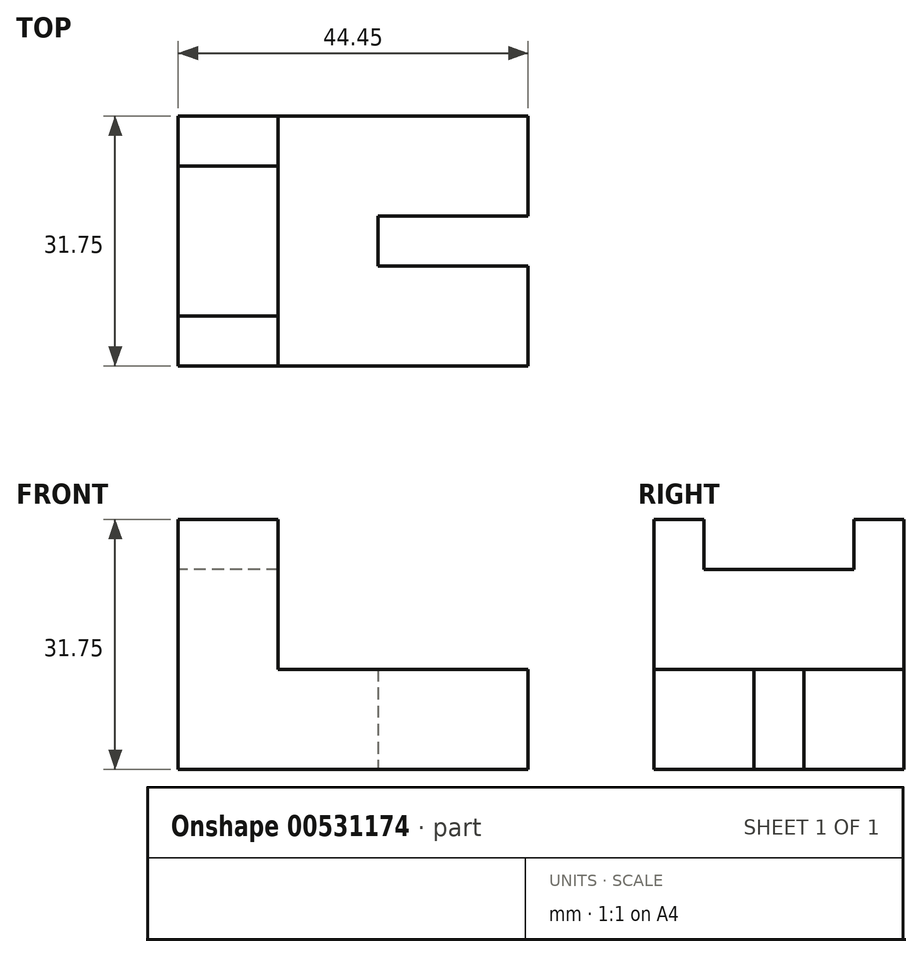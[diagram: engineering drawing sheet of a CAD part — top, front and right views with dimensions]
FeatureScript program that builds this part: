
annotation { "Feature Type Name" : "Feature", "Feature Type Description" : "" }
export const myFeature = defineFeature(function(context is Context, id is Id, definition is map)
    precondition{}
    {
        {
            var Q0;
            Q0=qCreatedBy(makeId("Front.planeOp"),FACE);
            var sketch = newSketch(context, id + "F0", { "sketchPlane" : qUnion([Q0])});
            skLineSegment(sketch, "E0", {"start": v(0, 0) * mm, "end": v(0, 31.75) * mm});
            skLineSegment(sketch, "E1", {"start": v(0, 31.75) * mm, "end": v(12.7, 31.75) * mm});
            skLineSegment(sketch, "E2", {"start": v(12.7, 31.75) * mm, "end": v(12.7, 12.7) * mm});
            skLineSegment(sketch, "E3", {"start": v(12.7, 12.7) * mm, "end": v(44.45, 12.7) * mm});
            skLineSegment(sketch, "E4", {"start": v(44.45, 12.7) * mm, "end": v(44.45, 0) * mm});
            skLineSegment(sketch, "E5", {"start": v(44.45, 0) * mm, "end": v(0, 0) * mm});
            skSolve(sketch);
        }
        {
            var Q0;
            Q0=qCreatedBy(makeId("Right.planeOp"),FACE);
            var sketch = newSketch(context, id + "F1", { "sketchPlane" : qUnion([Q0])});
            skLineSegment(sketch, "E6", {"start": v(0, 0) * mm, "end": v(0, 31.75) * mm});
            skLineSegment(sketch, "E7", {"start": v(0, 31.75) * mm, "end": v(-6.35, 31.75) * mm});
            skLineSegment(sketch, "E8", {"start": v(-6.35, 31.75) * mm, "end": v(-6.35, 25.4) * mm});
            skLineSegment(sketch, "E9", {"start": v(-6.35, 25.4) * mm, "end": v(-25.4, 25.4) * mm});
            skLineSegment(sketch, "E10", {"start": v(-25.4, 25.4) * mm, "end": v(-25.4, 31.75) * mm});
            skLineSegment(sketch, "E11", {"start": v(-25.4, 31.75) * mm, "end": v(-31.75, 31.75) * mm});
            skLineSegment(sketch, "E12", {"start": v(-25.4, 31.75) * mm, "end": v(-6.35, 31.75) * mm});
            skSolve(sketch);
        }
        {
            var Q0;
            Q0=makeQuery(id+"F0.imprint","IMPRINT",FACE,{"disambiguationData":[TD([[makeQuery(id+"F0.imprint","IMPRINT",EDGE,{"derivedFrom":sQuery(id+"F0.wireOp",EDGE,"E0")}),-1.0]])]});
            extrude(context, id + "F2", {"entities" : qUnion([Q0]), "depth" : 31.75 * mm, "offsetDistance" : 25.4 * mm});
        }
        {
            var Q0;
            Q0=makeQuery(id+"F1.imprint","IMPRINT",FACE,{"disambiguationData":[TD([[makeQuery(id+"F1.imprint","IMPRINT",EDGE,{"derivedFrom":sQuery(id+"F1.wireOp",EDGE,"E8")}),-1.0]])]});
            extrude(context, id + "F3", {"entities" : qUnion([Q0]), "operationType" : NewBodyOperationType.REMOVE, "depth" : 27.7 * mm, "offsetDistance" : 25.4 * mm});
        }
        {
            var Q0;
            Q0=qCreatedBy(makeId("Top.planeOp"),FACE);
            var sketch = newSketch(context, id + "F4", { "sketchPlane" : qUnion([Q0])});
            skLineSegment(sketch, "E13", {"start": v(0, 0) * mm, "end": v(25.4, 0) * mm});
            skLineSegment(sketch, "E14", {"start": v(25.4, 0) * mm, "end": v(25.4, -12.7) * mm});
            skLineSegment(sketch, "E15", {"start": v(25.4, -12.7) * mm, "end": v(25.4, -19.05) * mm});
            skLineSegment(sketch, "E16", {"start": v(25.4, -19.05) * mm, "end": v(44.45, -19.05) * mm});
            skLineSegment(sketch, "E17", {"start": v(44.45, -19.05) * mm, "end": v(44.45, -12.7) * mm});
            skLineSegment(sketch, "E18", {"start": v(44.45, -12.7) * mm, "end": v(25.4, -12.7) * mm});
            skSolve(sketch);
        }
        {
            var Q0;
            Q0=makeQuery(id+"F4.imprint","IMPRINT",FACE,{"disambiguationData":[TD([[makeQuery(id+"F4.imprint","IMPRINT",EDGE,{"derivedFrom":sQuery(id+"F4.wireOp",EDGE,"E15")}),1.0]])]});
            extrude(context, id + "F5", {"entities" : qUnion([Q0]), "operationType" : NewBodyOperationType.REMOVE, "depth" : 72.31 * mm, "offsetDistance" : 25.4 * mm});
        }
    });
